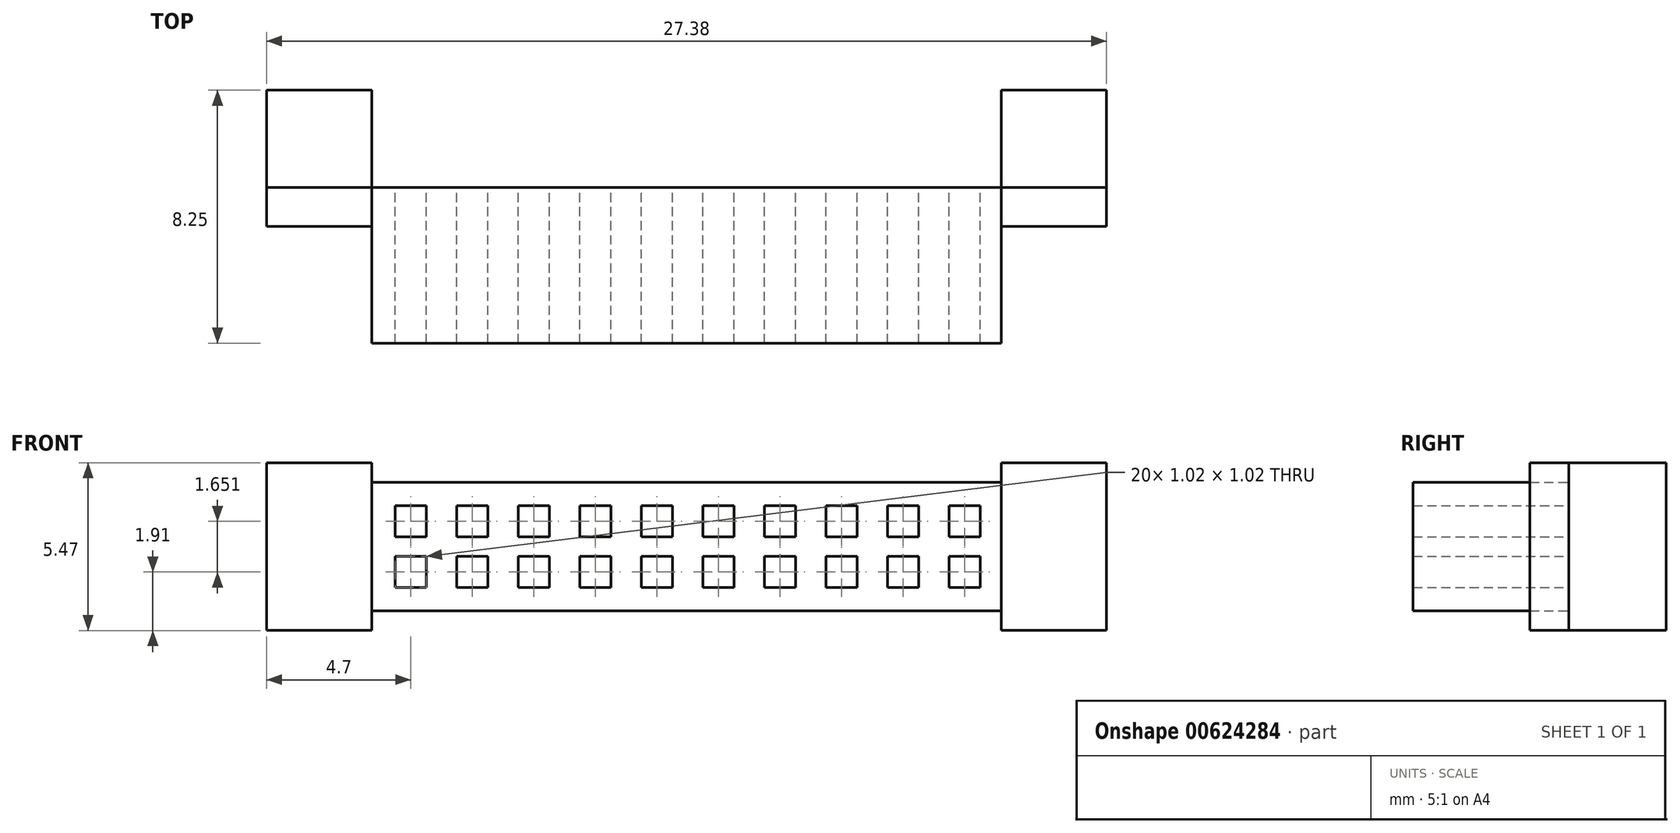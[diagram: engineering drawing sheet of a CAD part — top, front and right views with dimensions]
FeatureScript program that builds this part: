
annotation { "Feature Type Name" : "Feature", "Feature Type Description" : "" }
export const myFeature = defineFeature(function(context is Context, id is Id, definition is map)
    precondition{}
    {
        {
            var Q0;
            Q0=qCreatedBy(makeId("Front.planeOp"),FACE);
            var sketch = newSketch(context, id + "F0", { "sketchPlane" : qUnion([Q0])});
            skLineSegment(sketch, "E0.bottom", {"start": v(0, 0) * mm, "end": v(20.52, 0) * mm});
            skLineSegment(sketch, "E0.top", {"start": v(0, 4.2) * mm, "end": v(20.52, 4.2) * mm});
            skLineSegment(sketch, "E0.left", {"start": v(0, 0) * mm, "end": v(0, 4.2) * mm});
            skLineSegment(sketch, "E0.right", {"start": v(20.52, 0) * mm, "end": v(20.52, 4.2) * mm});
            skLineSegment(sketch, "E1.bottom", {"start": v(0.76, 3.43) * mm, "end": v(1.78, 3.43) * mm});
            skLineSegment(sketch, "E1.top", {"start": v(0.76, 2.41) * mm, "end": v(1.78, 2.41) * mm});
            skLineSegment(sketch, "E1.left", {"start": v(0.76, 3.43) * mm, "end": v(0.76, 2.41) * mm});
            skLineSegment(sketch, "E1.right", {"start": v(1.78, 3.43) * mm, "end": v(1.78, 2.41) * mm});
            skLineSegment(sketch, "E2.bottom", {"start": v(0.76, 1.78) * mm, "end": v(1.78, 1.78) * mm});
            skLineSegment(sketch, "E2.top", {"start": v(0.76, 0.76) * mm, "end": v(1.78, 0.76) * mm});
            skLineSegment(sketch, "E2.left", {"start": v(0.76, 1.78) * mm, "end": v(0.76, 0.76) * mm});
            skLineSegment(sketch, "E2.right", {"start": v(1.78, 1.78) * mm, "end": v(1.78, 0.76) * mm});
            skLineSegment(sketch, "E3.2.0.0", {"start": v(51.56, 3.43) * mm, "end": v(52.58, 3.43) * mm});
            skLineSegment(sketch, "E3.2.0.1", {"start": v(51.56, 2.41) * mm, "end": v(52.58, 2.41) * mm});
            skLineSegment(sketch, "E3.2.0.2", {"start": v(51.56, 3.43) * mm, "end": v(51.56, 2.41) * mm});
            skLineSegment(sketch, "E3.2.0.3", {"start": v(52.58, 3.43) * mm, "end": v(52.58, 2.41) * mm});
            skLineSegment(sketch, "E3.2.0.4", {"start": v(51.56, 1.78) * mm, "end": v(52.58, 1.78) * mm});
            skLineSegment(sketch, "E3.2.0.5", {"start": v(51.56, 0.76) * mm, "end": v(52.58, 0.76) * mm});
            skLineSegment(sketch, "E3.2.0.6", {"start": v(51.56, 1.78) * mm, "end": v(51.56, 0.76) * mm});
            skLineSegment(sketch, "E3.2.0.7", {"start": v(52.58, 1.78) * mm, "end": v(52.58, 0.76) * mm});
            skLineSegment(sketch, "E4.2.0.1", {"start": v(51.56, 0.76) * mm, "end": v(76.96, 0.76) * mm, "construction": true});
            skLineSegment(sketch, "E5.1.0.0", {"start": v(2.77, 3.43) * mm, "end": v(3.78, 3.43) * mm});
            skLineSegment(sketch, "E5.1.0.1", {"start": v(2.77, 3.43) * mm, "end": v(2.77, 2.41) * mm});
            skLineSegment(sketch, "E5.1.0.2", {"start": v(2.77, 2.41) * mm, "end": v(3.78, 2.41) * mm});
            skLineSegment(sketch, "E5.1.0.3", {"start": v(3.78, 3.43) * mm, "end": v(3.78, 2.41) * mm});
            skLineSegment(sketch, "E5.2.0.0", {"start": v(4.78, 3.43) * mm, "end": v(5.8, 3.43) * mm});
            skLineSegment(sketch, "E5.2.0.1", {"start": v(4.78, 3.43) * mm, "end": v(4.78, 2.41) * mm});
            skLineSegment(sketch, "E5.2.0.2", {"start": v(4.78, 2.41) * mm, "end": v(5.8, 2.41) * mm});
            skLineSegment(sketch, "E5.2.0.3", {"start": v(5.8, 3.43) * mm, "end": v(5.8, 2.41) * mm});
            skLineSegment(sketch, "E5.3.0.0", {"start": v(6.78, 3.43) * mm, "end": v(7.8, 3.43) * mm});
            skLineSegment(sketch, "E5.3.0.1", {"start": v(6.78, 3.43) * mm, "end": v(6.78, 2.41) * mm});
            skLineSegment(sketch, "E5.3.0.2", {"start": v(6.78, 2.41) * mm, "end": v(7.8, 2.41) * mm});
            skLineSegment(sketch, "E5.3.0.3", {"start": v(7.8, 3.43) * mm, "end": v(7.8, 2.41) * mm});
            skLineSegment(sketch, "E5.4.0.0", {"start": v(8.79, 3.43) * mm, "end": v(9.8, 3.43) * mm});
            skLineSegment(sketch, "E5.4.0.1", {"start": v(8.79, 3.43) * mm, "end": v(8.79, 2.41) * mm});
            skLineSegment(sketch, "E5.4.0.2", {"start": v(8.79, 2.41) * mm, "end": v(9.8, 2.41) * mm});
            skLineSegment(sketch, "E5.4.0.3", {"start": v(9.8, 3.43) * mm, "end": v(9.8, 2.41) * mm});
            skLineSegment(sketch, "E5.5.0.0", {"start": v(10.8, 3.43) * mm, "end": v(11.81, 3.43) * mm});
            skLineSegment(sketch, "E5.5.0.1", {"start": v(10.8, 3.43) * mm, "end": v(10.8, 2.41) * mm});
            skLineSegment(sketch, "E5.5.0.2", {"start": v(10.8, 2.41) * mm, "end": v(11.81, 2.41) * mm});
            skLineSegment(sketch, "E5.5.0.3", {"start": v(11.81, 3.43) * mm, "end": v(11.81, 2.41) * mm});
            skLineSegment(sketch, "E5.6.0.0", {"start": v(12.8, 3.43) * mm, "end": v(13.82, 3.43) * mm});
            skLineSegment(sketch, "E5.6.0.1", {"start": v(12.8, 3.43) * mm, "end": v(12.8, 2.41) * mm});
            skLineSegment(sketch, "E5.6.0.2", {"start": v(12.8, 2.41) * mm, "end": v(13.82, 2.41) * mm});
            skLineSegment(sketch, "E5.6.0.3", {"start": v(13.82, 3.43) * mm, "end": v(13.82, 2.41) * mm});
            skLineSegment(sketch, "E5.7.0.0", {"start": v(14.8, 3.43) * mm, "end": v(15.82, 3.43) * mm});
            skLineSegment(sketch, "E5.7.0.1", {"start": v(14.8, 3.43) * mm, "end": v(14.8, 2.41) * mm});
            skLineSegment(sketch, "E5.7.0.2", {"start": v(14.8, 2.41) * mm, "end": v(15.82, 2.41) * mm});
            skLineSegment(sketch, "E5.7.0.3", {"start": v(15.82, 3.43) * mm, "end": v(15.82, 2.41) * mm});
            skLineSegment(sketch, "E5.8.0.0", {"start": v(16.81, 3.43) * mm, "end": v(17.83, 3.43) * mm});
            skLineSegment(sketch, "E5.8.0.1", {"start": v(16.81, 3.43) * mm, "end": v(16.81, 2.41) * mm});
            skLineSegment(sketch, "E5.8.0.2", {"start": v(16.81, 2.41) * mm, "end": v(17.83, 2.41) * mm});
            skLineSegment(sketch, "E5.8.0.3", {"start": v(17.83, 3.43) * mm, "end": v(17.83, 2.41) * mm});
            skLineSegment(sketch, "E5.9.0.0", {"start": v(18.82, 3.43) * mm, "end": v(19.84, 3.43) * mm});
            skLineSegment(sketch, "E5.9.0.1", {"start": v(18.82, 3.43) * mm, "end": v(18.82, 2.41) * mm});
            skLineSegment(sketch, "E5.9.0.2", {"start": v(18.82, 2.41) * mm, "end": v(19.84, 2.41) * mm});
            skLineSegment(sketch, "E5.9.0.3", {"start": v(19.84, 3.43) * mm, "end": v(19.84, 2.41) * mm});
            skLineSegment(sketch, "E5.direction1", {"start": v(0.76, 3.43) * mm, "end": v(2.77, 3.43) * mm, "construction": true});
            skLineSegment(sketch, "E6.1.0.0", {"start": v(3.78, 1.78) * mm, "end": v(3.78, 0.76) * mm});
            skLineSegment(sketch, "E6.1.0.1", {"start": v(2.77, 1.78) * mm, "end": v(3.78, 1.78) * mm});
            skLineSegment(sketch, "E6.1.0.2", {"start": v(2.77, 0.76) * mm, "end": v(3.78, 0.76) * mm});
            skLineSegment(sketch, "E6.1.0.3", {"start": v(2.77, 1.78) * mm, "end": v(2.77, 0.76) * mm});
            skLineSegment(sketch, "E6.2.0.0", {"start": v(5.8, 1.78) * mm, "end": v(5.8, 0.76) * mm});
            skLineSegment(sketch, "E6.2.0.1", {"start": v(4.78, 1.78) * mm, "end": v(5.8, 1.78) * mm});
            skLineSegment(sketch, "E6.2.0.2", {"start": v(4.78, 0.76) * mm, "end": v(5.8, 0.76) * mm});
            skLineSegment(sketch, "E6.2.0.3", {"start": v(4.78, 1.78) * mm, "end": v(4.78, 0.76) * mm});
            skLineSegment(sketch, "E6.direction1", {"start": v(0.76, 0.76) * mm, "end": v(2.77, 0.76) * mm, "construction": true});
            skLineSegment(sketch, "E7.0.3.0", {"start": v(7.8, 1.78) * mm, "end": v(7.8, 0.76) * mm});
            skLineSegment(sketch, "E7.3.3.0", {"start": v(6.78, 1.78) * mm, "end": v(7.8, 1.78) * mm});
            skLineSegment(sketch, "E7.6.3.0", {"start": v(6.78, 0.76) * mm, "end": v(7.8, 0.76) * mm});
            skLineSegment(sketch, "E7.9.3.0", {"start": v(6.78, 1.78) * mm, "end": v(6.78, 0.76) * mm});
            skLineSegment(sketch, "E7.0.4.0", {"start": v(9.8, 1.78) * mm, "end": v(9.8, 0.76) * mm});
            skLineSegment(sketch, "E7.3.4.0", {"start": v(8.79, 1.78) * mm, "end": v(9.8, 1.78) * mm});
            skLineSegment(sketch, "E7.6.4.0", {"start": v(8.79, 0.76) * mm, "end": v(9.8, 0.76) * mm});
            skLineSegment(sketch, "E7.9.4.0", {"start": v(8.79, 1.78) * mm, "end": v(8.79, 0.76) * mm});
            skLineSegment(sketch, "E7.0.5.0", {"start": v(11.81, 1.78) * mm, "end": v(11.81, 0.76) * mm});
            skLineSegment(sketch, "E7.3.5.0", {"start": v(10.8, 1.78) * mm, "end": v(11.81, 1.78) * mm});
            skLineSegment(sketch, "E7.6.5.0", {"start": v(10.8, 0.76) * mm, "end": v(11.81, 0.76) * mm});
            skLineSegment(sketch, "E7.9.5.0", {"start": v(10.8, 1.78) * mm, "end": v(10.8, 0.76) * mm});
            skLineSegment(sketch, "E7.0.6.0", {"start": v(13.82, 1.78) * mm, "end": v(13.82, 0.76) * mm});
            skLineSegment(sketch, "E7.3.6.0", {"start": v(12.8, 1.78) * mm, "end": v(13.82, 1.78) * mm});
            skLineSegment(sketch, "E7.6.6.0", {"start": v(12.8, 0.76) * mm, "end": v(13.82, 0.76) * mm});
            skLineSegment(sketch, "E7.9.6.0", {"start": v(12.8, 1.78) * mm, "end": v(12.8, 0.76) * mm});
            skLineSegment(sketch, "E7.0.7.0", {"start": v(15.82, 1.78) * mm, "end": v(15.82, 0.76) * mm});
            skLineSegment(sketch, "E7.3.7.0", {"start": v(14.8, 1.78) * mm, "end": v(15.82, 1.78) * mm});
            skLineSegment(sketch, "E7.6.7.0", {"start": v(14.8, 0.76) * mm, "end": v(15.82, 0.76) * mm});
            skLineSegment(sketch, "E7.9.7.0", {"start": v(14.8, 1.78) * mm, "end": v(14.8, 0.76) * mm});
            skLineSegment(sketch, "E7.0.8.0", {"start": v(17.83, 1.78) * mm, "end": v(17.83, 0.76) * mm});
            skLineSegment(sketch, "E7.3.8.0", {"start": v(16.81, 1.78) * mm, "end": v(17.83, 1.78) * mm});
            skLineSegment(sketch, "E7.6.8.0", {"start": v(16.81, 0.76) * mm, "end": v(17.83, 0.76) * mm});
            skLineSegment(sketch, "E7.9.8.0", {"start": v(16.81, 1.78) * mm, "end": v(16.81, 0.76) * mm});
            skLineSegment(sketch, "E7.0.9.0", {"start": v(19.84, 1.78) * mm, "end": v(19.84, 0.76) * mm});
            skLineSegment(sketch, "E7.3.9.0", {"start": v(18.82, 1.78) * mm, "end": v(19.84, 1.78) * mm});
            skLineSegment(sketch, "E7.6.9.0", {"start": v(18.82, 0.76) * mm, "end": v(19.84, 0.76) * mm});
            skLineSegment(sketch, "E7.9.9.0", {"start": v(18.82, 1.78) * mm, "end": v(18.82, 0.76) * mm});
            skSolve(sketch);
        }
        {
            var Q0;
            Q0=makeQuery(id+"F0.imprint","IMPRINT",FACE,{"disambiguationData":[TD([[makeQuery(id+"F0.imprint","IMPRINT",EDGE,{"derivedFrom":sQuery(id+"F0.wireOp",EDGE,"E0.bottom")}),1.0]])]});
            extrude(context, id + "F1", {"entities" : qUnion([Q0]), "depth" : 5.08 * mm, "offsetDistance" : 25.4 * mm});
        }
        {
            var Q0;
            Q0=makeQuery(id+"F1.opExtrude","CAP_FACE",FACE,{"disambiguationData":[OSD([sQuery(id+"F0.wireOp",EDGE,"E0.bottom"),sQuery(id+"F0.wireOp",EDGE,"E0.top"),sQuery(id+"F0.wireOp",EDGE,"E0.left"),sQuery(id+"F0.wireOp",EDGE,"E0.right"),sQuery(id+"F0.wireOp",EDGE,"E1.bottom"),sQuery(id+"F0.wireOp",EDGE,"E1.top"),sQuery(id+"F0.wireOp",EDGE,"E1.left"),sQuery(id+"F0.wireOp",EDGE,"E1.right"),sQuery(id+"F0.wireOp",EDGE,"E2.bottom"),sQuery(id+"F0.wireOp",EDGE,"E2.top"),sQuery(id+"F0.wireOp",EDGE,"E2.left"),sQuery(id+"F0.wireOp",EDGE,"E2.right"),sQuery(id+"F0.wireOp",EDGE,"E5.1.0.0"),sQuery(id+"F0.wireOp",EDGE,"E5.1.0.1"),sQuery(id+"F0.wireOp",EDGE,"E5.1.0.2"),sQuery(id+"F0.wireOp",EDGE,"E5.1.0.3"),sQuery(id+"F0.wireOp",EDGE,"E5.2.0.0"),sQuery(id+"F0.wireOp",EDGE,"E5.2.0.1"),sQuery(id+"F0.wireOp",EDGE,"E5.2.0.2"),sQuery(id+"F0.wireOp",EDGE,"E5.2.0.3"),sQuery(id+"F0.wireOp",EDGE,"E5.3.0.0"),sQuery(id+"F0.wireOp",EDGE,"E5.3.0.1"),sQuery(id+"F0.wireOp",EDGE,"E5.3.0.2"),sQuery(id+"F0.wireOp",EDGE,"E5.3.0.3"),sQuery(id+"F0.wireOp",EDGE,"E5.4.0.0"),sQuery(id+"F0.wireOp",EDGE,"E5.4.0.1"),sQuery(id+"F0.wireOp",EDGE,"E5.4.0.2"),sQuery(id+"F0.wireOp",EDGE,"E5.4.0.3"),sQuery(id+"F0.wireOp",EDGE,"E5.5.0.0"),sQuery(id+"F0.wireOp",EDGE,"E5.5.0.1"),sQuery(id+"F0.wireOp",EDGE,"E5.5.0.2"),sQuery(id+"F0.wireOp",EDGE,"E5.5.0.3"),sQuery(id+"F0.wireOp",EDGE,"E5.6.0.0"),sQuery(id+"F0.wireOp",EDGE,"E5.6.0.1"),sQuery(id+"F0.wireOp",EDGE,"E5.6.0.2"),sQuery(id+"F0.wireOp",EDGE,"E5.6.0.3"),sQuery(id+"F0.wireOp",EDGE,"E5.7.0.0"),sQuery(id+"F0.wireOp",EDGE,"E5.7.0.1"),sQuery(id+"F0.wireOp",EDGE,"E5.7.0.2"),sQuery(id+"F0.wireOp",EDGE,"E5.7.0.3"),sQuery(id+"F0.wireOp",EDGE,"E5.8.0.0"),sQuery(id+"F0.wireOp",EDGE,"E5.8.0.1"),sQuery(id+"F0.wireOp",EDGE,"E5.8.0.2"),sQuery(id+"F0.wireOp",EDGE,"E5.8.0.3"),sQuery(id+"F0.wireOp",EDGE,"E5.9.0.0"),sQuery(id+"F0.wireOp",EDGE,"E5.9.0.1"),sQuery(id+"F0.wireOp",EDGE,"E5.9.0.2"),sQuery(id+"F0.wireOp",EDGE,"E5.9.0.3"),sQuery(id+"F0.wireOp",EDGE,"E6.1.0.0"),sQuery(id+"F0.wireOp",EDGE,"E6.1.0.1"),sQuery(id+"F0.wireOp",EDGE,"E6.1.0.2"),sQuery(id+"F0.wireOp",EDGE,"E6.1.0.3"),sQuery(id+"F0.wireOp",EDGE,"E6.2.0.0"),sQuery(id+"F0.wireOp",EDGE,"E6.2.0.1"),sQuery(id+"F0.wireOp",EDGE,"E6.2.0.2"),sQuery(id+"F0.wireOp",EDGE,"E6.2.0.3"),sQuery(id+"F0.wireOp",EDGE,"E7.0.3.0"),sQuery(id+"F0.wireOp",EDGE,"E7.3.3.0"),sQuery(id+"F0.wireOp",EDGE,"E7.6.3.0"),sQuery(id+"F0.wireOp",EDGE,"E7.9.3.0"),sQuery(id+"F0.wireOp",EDGE,"E7.0.4.0"),sQuery(id+"F0.wireOp",EDGE,"E7.3.4.0"),sQuery(id+"F0.wireOp",EDGE,"E7.6.4.0"),sQuery(id+"F0.wireOp",EDGE,"E7.9.4.0"),sQuery(id+"F0.wireOp",EDGE,"E7.0.5.0"),sQuery(id+"F0.wireOp",EDGE,"E7.3.5.0"),sQuery(id+"F0.wireOp",EDGE,"E7.6.5.0"),sQuery(id+"F0.wireOp",EDGE,"E7.9.5.0"),sQuery(id+"F0.wireOp",EDGE,"E7.0.6.0"),sQuery(id+"F0.wireOp",EDGE,"E7.3.6.0"),sQuery(id+"F0.wireOp",EDGE,"E7.6.6.0"),sQuery(id+"F0.wireOp",EDGE,"E7.9.6.0"),sQuery(id+"F0.wireOp",EDGE,"E7.0.7.0"),sQuery(id+"F0.wireOp",EDGE,"E7.3.7.0"),sQuery(id+"F0.wireOp",EDGE,"E7.6.7.0"),sQuery(id+"F0.wireOp",EDGE,"E7.9.7.0"),sQuery(id+"F0.wireOp",EDGE,"E7.0.8.0"),sQuery(id+"F0.wireOp",EDGE,"E7.3.8.0"),sQuery(id+"F0.wireOp",EDGE,"E7.6.8.0"),sQuery(id+"F0.wireOp",EDGE,"E7.9.8.0"),sQuery(id+"F0.wireOp",EDGE,"E7.0.9.0"),sQuery(id+"F0.wireOp",EDGE,"E7.3.9.0"),sQuery(id+"F0.wireOp",EDGE,"E7.6.9.0"),sQuery(id+"F0.wireOp",EDGE,"E7.9.9.0")])],"isStart":true});
            var sketch = newSketch(context, id + "F2", { "sketchPlane" : qUnion([Q0])});
            skLineSegment(sketch, "E8.bottom", {"start": v(-23.95, 4.83) * mm, "end": v(-20.52, 4.83) * mm});
            skLineSegment(sketch, "E8.top", {"start": v(-23.95, -0.64) * mm, "end": v(-20.52, -0.64) * mm});
            skLineSegment(sketch, "E8.left", {"start": v(-23.95, 4.83) * mm, "end": v(-23.95, -0.64) * mm});
            skLineSegment(sketch, "E8.right", {"start": v(-20.52, 4.83) * mm, "end": v(-20.52, -0.64) * mm});
            skLineSegment(sketch, "E9.bottom", {"start": v(0, 4.83) * mm, "end": v(3.43, 4.83) * mm});
            skLineSegment(sketch, "E9.top", {"start": v(0, -0.64) * mm, "end": v(3.43, -0.64) * mm});
            skLineSegment(sketch, "E9.left", {"start": v(0, 4.83) * mm, "end": v(0, -0.64) * mm});
            skLineSegment(sketch, "E9.right", {"start": v(3.43, 4.83) * mm, "end": v(3.43, -0.64) * mm});
            skLineSegment(sketch, "E10", {"start": v(-23.95, 2.1) * mm, "end": v(-20.52, 2.1) * mm, "construction": true});
            skLineSegment(sketch, "E11", {"start": v(3.43, 2.1) * mm, "end": v(0, 2.1) * mm, "construction": true});
            skSolve(sketch);
        }
        {
            var Q0;
            {var subQ2=sQuery(id+"F2.wireOp",EDGE,"E8.bottom");Q0=makeQuery(id+"F2.imprint","IMPRINT",FACE,{"disambiguationData":[TD([[makeQuery(id+"F2.imprint","IMPRINT",EDGE,{"derivedFrom":subQ2}),-1.0]])]});}
            var Q1;
            {var subQ3=sQuery(id+"F2.wireOp",EDGE,"E9.bottom");Q1=makeQuery(id+"F2.imprint","IMPRINT",FACE,{"disambiguationData":[TD([[makeQuery(id+"F2.imprint","IMPRINT",EDGE,{"derivedFrom":subQ3}),-1.0]])]});}
            extrude(context, id + "F3", {"entities" : qUnion([Q0, Q1]), "depth" : 3.17 * mm, "offsetDistance" : 25.4 * mm});
        }
        {
            var Q0;
            Q0=makeQuery(id+"F3.opExtrude","CAP_FACE",FACE,{"disambiguationData":[OSD([sQuery(id+"F2.wireOp",EDGE,"E8.bottom"),sQuery(id+"F2.wireOp",EDGE,"E8.top"),sQuery(id+"F2.wireOp",EDGE,"E8.left"),sQuery(id+"F2.wireOp",EDGE,"E8.right")])],"isStart":true});
            var Q1;
            Q1=makeQuery(id+"F3.opExtrude","CAP_FACE",FACE,{"disambiguationData":[OSD([sQuery(id+"F2.wireOp",EDGE,"E9.bottom"),sQuery(id+"F2.wireOp",EDGE,"E9.top"),sQuery(id+"F2.wireOp",EDGE,"E9.left"),sQuery(id+"F2.wireOp",EDGE,"E9.right")])],"isStart":true});
            extrude(context, id + "F4", {"entities" : qUnion([Q0, Q1]), "depth" : 1.27 * mm, "offsetDistance" : 25.4 * mm});
        }
    });
